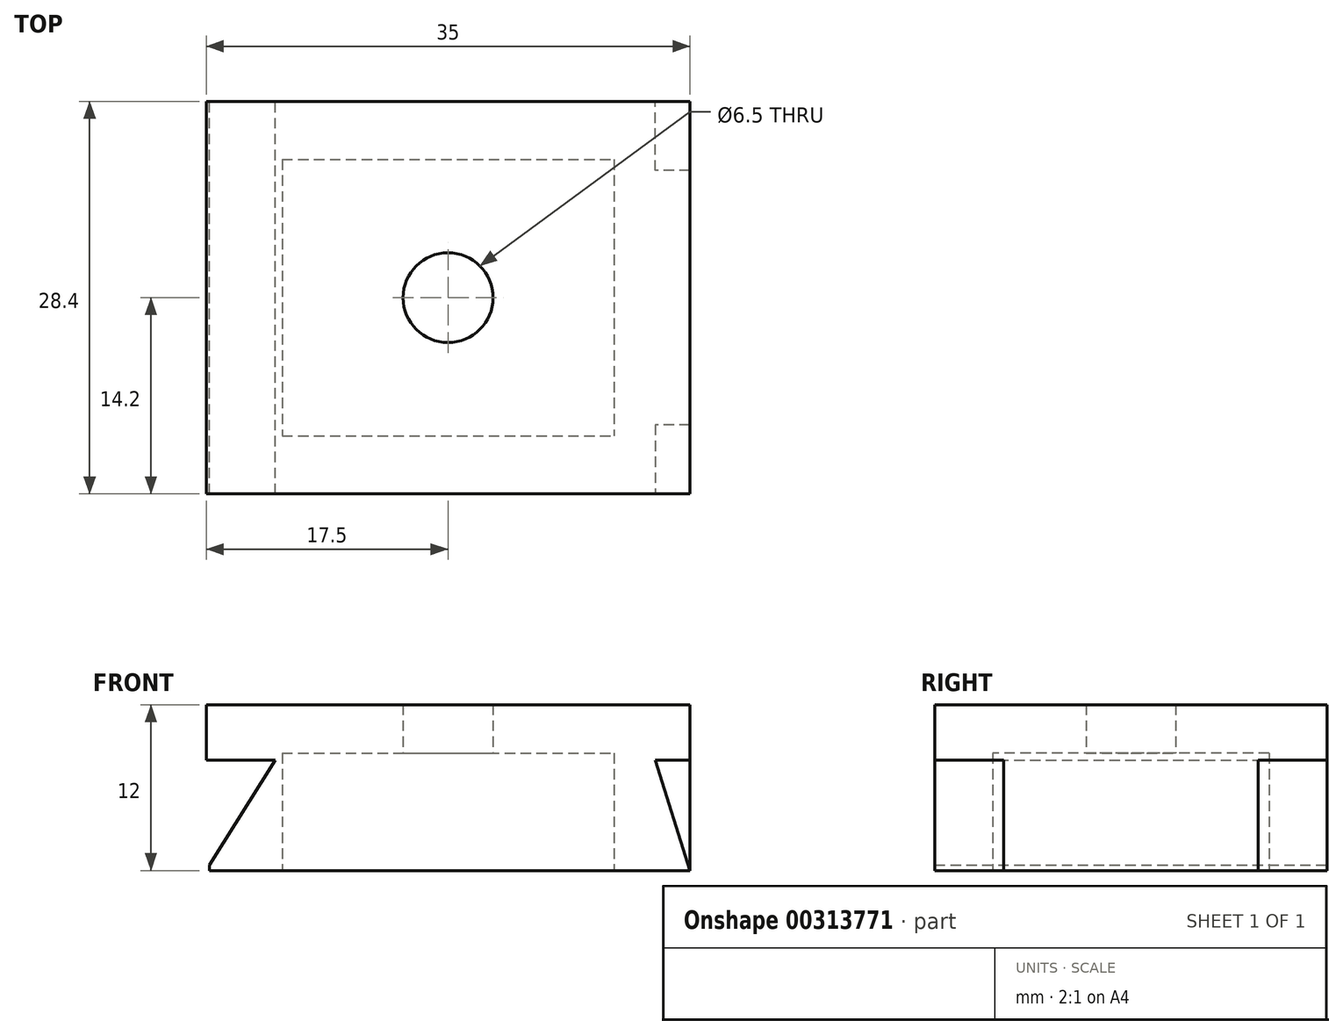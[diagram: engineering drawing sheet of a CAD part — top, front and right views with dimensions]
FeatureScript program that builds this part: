
annotation { "Feature Type Name" : "Feature", "Feature Type Description" : "" }
export const myFeature = defineFeature(function(context is Context, id is Id, definition is map)
    precondition{}
    {
        {
            var Q0;
            Q0=qCreatedBy(makeId("Top.planeOp"),FACE);
            var sketch = newSketch(context, id + "F0", { "sketchPlane" : qUnion([Q0])});
            skLineSegment(sketch, "E0.bottom", {"start": v(17.5, 14.2) * mm, "end": v(-17.5, 14.2) * mm});
            skLineSegment(sketch, "E0.top", {"start": v(17.5, -14.2) * mm, "end": v(-17.5, -14.2) * mm});
            skLineSegment(sketch, "E0.left", {"start": v(17.5, 14.2) * mm, "end": v(17.5, -14.2) * mm});
            skLineSegment(sketch, "E0.right", {"start": v(-17.5, 14.2) * mm, "end": v(-17.5, -14.2) * mm});
            skPoint(sketch, "E0.middle", {"position": v(0, 0) * mm});
            skSolve(sketch);
        }
        {
            var Q0;
            Q0 = qSketchRegion(id + "F0", true);
            extrude(context, id + "F1", {"entities" : qUnion([Q0]), "depth" : 12 * mm});
        }
        {
            var Q0;
            Q0=makeQuery(id+"F1.opExtrude","SWEPT_FACE",FACE,{"disambiguationData":[OSD([sQuery(id+"F0.wireOp",EDGE,"E0.top")])]});
            var sketch = newSketch(context, id + "F2", { "sketchPlane" : qUnion([Q0])});
            skLineSegment(sketch, "E1", {"start": v(17.5, 0) * mm, "end": v(15, 8) * mm});
            skLineSegment(sketch, "E2", {"start": v(15, 8) * mm, "end": v(17.5, 8) * mm});
            skLineSegment(sketch, "E3", {"start": v(17.5, 8) * mm, "end": v(17.5, 0) * mm});
            skSolve(sketch);
        }
        {
            var Q0;
            Q0 = qSketchRegion(id + "F2", true);
            extrude(context, id + "F3", {"entities" : qUnion([Q0]), "operationType" : NewBodyOperationType.REMOVE, "oppositeDirection" : true, "depth" : 5 * mm});
        }
        {
            var Q0;
            Q0=makeQuery(id+"F1.opExtrude","SWEPT_FACE",FACE,{"disambiguationData":[OSD([sQuery(id+"F0.wireOp",EDGE,"E0.bottom")])]});
            var sketch = newSketch(context, id + "F4", { "sketchPlane" : qUnion([Q0])});
            skLineSegment(sketch, "E4", {"start": v(-17.5, 8) * mm, "end": v(-17.5, 0) * mm});
            skLineSegment(sketch, "E5.MirrorCS", {"start": v(-15, 8) * mm, "end": v(-17.5, 8) * mm});
            skLineSegment(sketch, "E6", {"start": v(-17.5, 0) * mm, "end": v(-15, 8) * mm});
            skSolve(sketch);
        }
        {
            var Q0;
            Q0 = qSketchRegion(id + "F4", true);
            extrude(context, id + "F5", {"entities" : qUnion([Q0]), "operationType" : NewBodyOperationType.REMOVE, "oppositeDirection" : true, "depth" : 5 * mm});
        }
        {
            var Q0;
            Q0=makeQuery(id+"F1.opExtrude","SWEPT_FACE",FACE,{"disambiguationData":[OSD([sQuery(id+"F0.wireOp",EDGE,"E0.bottom")])]});
            var sketch = newSketch(context, id + "F6", { "sketchPlane" : qUnion([Q0])});
            skLineSegment(sketch, "E7", {"start": v(17.5, 0) * mm, "end": v(12.5, 8) * mm});
            skLineSegment(sketch, "E8", {"start": v(12.5, 8) * mm, "end": v(17.5, 8) * mm});
            skLineSegment(sketch, "E9", {"start": v(17.5, 8) * mm, "end": v(17.5, 0) * mm});
            skSolve(sketch);
        }
        {
            var Q0;
            Q0=makeQuery(id+"F6.imprint","IMPRINT",FACE,{"disambiguationData":[TD([[makeQuery(id+"F6.imprint","IMPRINT",EDGE,{"derivedFrom":sQuery(id+"F6.wireOp",EDGE,"E7")}),-1.0]])]});
            extrude(context, id + "F7", {"entities" : qUnion([Q0]), "operationType" : NewBodyOperationType.REMOVE, "oppositeDirection" : true, "depth" : 36.3 * mm});
        }
        {
            var Q0;
            Q0=makeQuery(id+"F1.opExtrude","CAP_FACE",FACE,{"disambiguationData":[OSD([sQuery(id+"F0.wireOp",EDGE,"E0.bottom"),sQuery(id+"F0.wireOp",EDGE,"E0.top"),sQuery(id+"F0.wireOp",EDGE,"E0.left"),sQuery(id+"F0.wireOp",EDGE,"E0.right")])],"isStart":true});
            var sketch = newSketch(context, id + "F8", { "sketchPlane" : qUnion([Q0])});
            skLineSegment(sketch, "E10.bottom", {"start": v(-12, -10) * mm, "end": v(12, -10) * mm});
            skLineSegment(sketch, "E10.top", {"start": v(-12, 10) * mm, "end": v(12, 10) * mm});
            skLineSegment(sketch, "E10.left", {"start": v(-12, -10) * mm, "end": v(-12, 10) * mm});
            skLineSegment(sketch, "E10.right", {"start": v(12, -10) * mm, "end": v(12, 10) * mm});
            skPoint(sketch, "E10.middle", {"position": v(0, 0) * mm});
            skSolve(sketch);
        }
        {
            var Q0;
            Q0=makeQuery(id+"F8.imprint","IMPRINT",FACE,{"disambiguationData":[TD([[makeQuery(id+"F8.imprint","IMPRINT",EDGE,{"derivedFrom":sQuery(id+"F8.wireOp",EDGE,"E10.bottom")}),1.0]])]});
            extrude(context, id + "F9", {"entities" : qUnion([Q0]), "operationType" : NewBodyOperationType.REMOVE, "oppositeDirection" : true, "depth" : 8.5 * mm});
        }
        {
            var Q0;
            Q0=makeQuery(id+"F9.boolean.opBoolean","COPY",FACE,{"derivedFrom":makeQuery(id+"F9.opExtrude","CAP_FACE",FACE,{"disambiguationData":[OSD([sQuery(id+"F8.wireOp",EDGE,"E10.bottom"),sQuery(id+"F8.wireOp",EDGE,"E10.top"),sQuery(id+"F8.wireOp",EDGE,"E10.left"),sQuery(id+"F8.wireOp",EDGE,"E10.right")])],"isStart":false})});
            var sketch = newSketch(context, id + "F10", { "sketchPlane" : qUnion([Q0])});
            skCircle(sketch, "E11", {"center": v(0, 0) * mm, "radius": 3.25 * mm});
            skSolve(sketch);
        }
        {
            var Q0;
            Q0=makeQuery(id+"F10.imprint","IMPRINT",FACE,{"disambiguationData":[TD([[makeQuery(id+"F10.imprint","IMPRINT",EDGE,{"derivedFrom":sQuery(id+"F10.wireOp",EDGE,"E11")}),1.0]])]});
            extrude(context, id + "F11", {"entities" : qUnion([Q0]), "operationType" : NewBodyOperationType.REMOVE, "oppositeDirection" : true, "depth" : 25 * mm});
        }
        {
            var Q0;
            Q0=makeQuery(id+"F1.opExtrude","SWEPT_FACE",FACE,{"disambiguationData":[OSD([sQuery(id+"F0.wireOp",EDGE,"E0.bottom")])]});
            var sketch = newSketch(context, id + "F12", { "sketchPlane" : qUnion([Q0])});
            skLineSegment(sketch, "E12", {"start": v(17.5, 0) * mm, "end": v(17.25, 0) * mm});
            skLineSegment(sketch, "E13", {"start": v(17.25, 0) * mm, "end": v(17.25, 2.17) * mm});
            skLineSegment(sketch, "E14", {"start": v(17.25, 2.17) * mm, "end": v(17.5, 2.17) * mm});
            skLineSegment(sketch, "E15", {"start": v(17.5, 2.17) * mm, "end": v(17.5, 0) * mm});
            skSolve(sketch);
        }
        {
            var Q0;
            {var subQ0=sQuery(id+"F12.wireOp",EDGE,"E12");Q0=makeQuery(id+"F12.imprint","IMPRINT",FACE,{"disambiguationData":[TD([[makeQuery(id+"F12.imprint","IMPRINT",EDGE,{"derivedFrom":subQ0}),1.0]])]});}
            var Q1;
            Q1=makeQuery(id+"F1.opExtrude","SWEPT_FACE",FACE,{"disambiguationData":[OSD([sQuery(id+"F0.wireOp",EDGE,"E0.top")])]});
            extrude(context, id + "F13", {"entities" : qUnion([Q0]), "operationType" : NewBodyOperationType.REMOVE, "endBound" : BoundingType.UP_TO_SURFACE, "oppositeDirection" : true, "endBoundEntityFace" : qUnion([Q1]), "depth" : 31 * mm});
        }
    });
